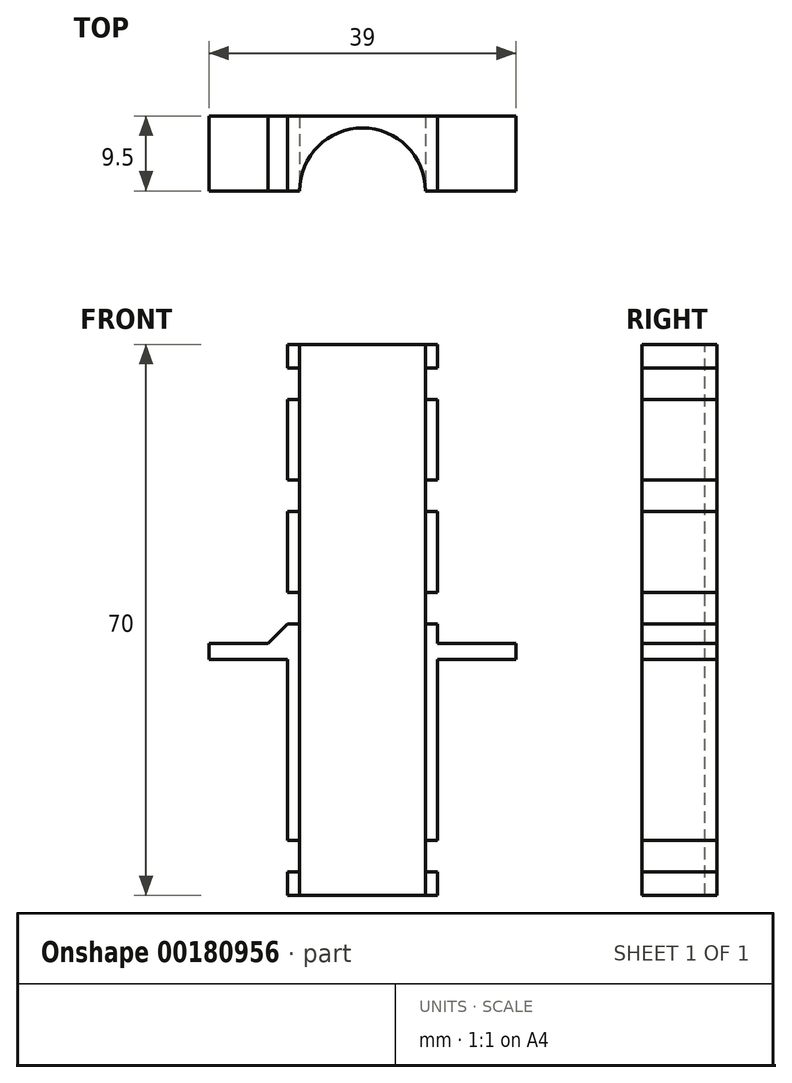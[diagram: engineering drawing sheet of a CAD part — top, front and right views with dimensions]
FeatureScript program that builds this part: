
annotation { "Feature Type Name" : "Feature", "Feature Type Description" : "" }
export const myFeature = defineFeature(function(context is Context, id is Id, definition is map)
    precondition{}
    {
        {
            var Q0;
            Q0=qCreatedBy(makeId("Top.planeOp"),FACE);
            var sketch = newSketch(context, id + "F0", { "sketchPlane" : qUnion([Q0])});
            skArc(sketch, "E0", {"start": v(-8, 0) * mm, "mid": v(0, 8) * mm, "end": v(8, 0) * mm});
            skLineSegment(sketch, "E1", {"start": v(-8, 0) * mm, "end": v(-9.5, 0) * mm});
            skLineSegment(sketch, "E2", {"start": v(8, 0) * mm, "end": v(9.5, 0) * mm});
            skLineSegment(sketch, "E3", {"start": v(-9.5, 0) * mm, "end": v(-9.5, 9.5) * mm});
            skLineSegment(sketch, "E4", {"start": v(-9.5, 9.5) * mm, "end": v(9.5, 9.5) * mm});
            skLineSegment(sketch, "E5", {"start": v(9.5, 9.5) * mm, "end": v(9.5, 0) * mm});
            skSolve(sketch);
        }
        {
            var Q0;
            Q0=qSketchRegion(id+"F0",true);
            extrude(context, id + "F1", {"entities" : qUnion([Q0]), "oppositeDirection" : true, "depth" : 40 * mm});
        }
        {
            var Q0;
            Q0=qCreatedBy(makeId("Top.planeOp"),FACE);
            cPlane(context, id + "F2", {"entities" : qUnion([Q0]), "cplaneType" : CPlaneType.OFFSET, "offset" : 10 * mm, "oppositeDirection" : true, "width" : 150 * mm, "height" : 150 * mm});
        }
        {
            var Q0;
            Q0=qCreatedBy(id+"F2.planeOp",FACE);
            var sketch = newSketch(context, id + "F3", { "sketchPlane" : qUnion([Q0])});
            skLineSegment(sketch, "E6.bottom", {"start": v(-9.5, 0) * mm, "end": v(-19.5, 0) * mm});
            skLineSegment(sketch, "E6.top", {"start": v(-9.5, 9.5) * mm, "end": v(-19.5, 9.5) * mm});
            skLineSegment(sketch, "E6.left", {"start": v(-9.5, 0) * mm, "end": v(-9.5, 9.5) * mm});
            skLineSegment(sketch, "E6.right", {"start": v(-19.5, 0) * mm, "end": v(-19.5, 9.5) * mm});
            skLineSegment(sketch, "E7.MirrorCS", {"start": v(9.5, 0) * mm, "end": v(19.5, 0) * mm});
            skLineSegment(sketch, "E8.MirrorCS", {"start": v(19.5, 0) * mm, "end": v(19.5, 9.5) * mm});
            skLineSegment(sketch, "E9.MirrorCS", {"start": v(9.5, 9.5) * mm, "end": v(19.5, 9.5) * mm});
            skLineSegment(sketch, "E10.MirrorCS", {"start": v(9.5, 0) * mm, "end": v(9.5, 9.5) * mm});
            skPoint(sketch, "E11", {"position": v(0, 0) * mm});
            skSolve(sketch);
        }
        {
            var Q0;
            Q0=qSketchRegion(id+"F3",true);
            extrude(context, id + "F4", {"entities" : qUnion([Q0]), "operationType" : NewBodyOperationType.ADD, "depth" : 2 * mm});
        }
        {
            var Q0;
            Q0=makeQuery(id+"F1.opExtrude","CAP_FACE",FACE,{"disambiguationData":[OSD([sQuery(id+"F0.wireOp",EDGE,"E0"),sQuery(id+"F0.wireOp",EDGE,"E1"),sQuery(id+"F0.wireOp",EDGE,"E2"),sQuery(id+"F0.wireOp",EDGE,"E3"),sQuery(id+"F0.wireOp",EDGE,"E4"),sQuery(id+"F0.wireOp",EDGE,"E5")])],"isStart":true});
            extrude(context, id + "F5", {"entities" : qUnion([Q0]), "operationType" : NewBodyOperationType.ADD, "depth" : 30 * mm});
        }
        {
            var Q0;
            {var subQ0=sQuery(id+"F3.wireOp",EDGE,"E6.left");var subQ2=sQuery(id+"F0.wireOp",EDGE,"E1");Q0=makeQuery(id+"F4.boolean.opBoolean","SPLIT",FACE,{"disambiguationData":[TD([makeQuery(id+"F4.opExtrude","CAP_FACE",FACE,{"disambiguationData":[OSD([sQuery(id+"F3.wireOp",EDGE,"E6.bottom"),sQuery(id+"F3.wireOp",EDGE,"E6.top"),subQ0,sQuery(id+"F3.wireOp",EDGE,"E6.right")])],"isStart":true})])],"derivedFrom":makeQuery(id+"F1.opExtrude","SWEPT_FACE",FACE,{"disambiguationData":[OSD([subQ2])]})});}
            var sketch = newSketch(context, id + "F6", { "sketchPlane" : qUnion([Q0])});
            skLineSegment(sketch, "E12.bottom", {"start": v(-9.5, -1.5) * mm, "end": v(-8, -1.5) * mm});
            skLineSegment(sketch, "E12.top", {"start": v(-9.5, -5.5) * mm, "end": v(-8, -5.5) * mm});
            skLineSegment(sketch, "E12.left", {"start": v(-9.5, -1.5) * mm, "end": v(-9.5, -5.5) * mm});
            skLineSegment(sketch, "E12.right", {"start": v(-8, -1.5) * mm, "end": v(-8, -5.5) * mm});
            skPoint(sketch, "E13", {"position": v(-9.5, -3.5) * mm});
            skLineSegment(sketch, "E14.bottom", {"start": v(-9.5, -37) * mm, "end": v(-8, -37) * mm});
            skLineSegment(sketch, "E14.top", {"start": v(-9.5, -33) * mm, "end": v(-8, -33) * mm});
            skLineSegment(sketch, "E14.left", {"start": v(-9.5, -37) * mm, "end": v(-9.5, -33) * mm});
            skLineSegment(sketch, "E14.right", {"start": v(-8, -37) * mm, "end": v(-8, -33) * mm});
            skLineSegment(sketch, "E15", {"start": v(-8, -37) * mm, "end": v(-8, -40) * mm, "construction": true});
            skLineSegment(sketch, "E16.MirrorCS", {"start": v(9.5, -1.5) * mm, "end": v(8, -1.5) * mm});
            skLineSegment(sketch, "E17.MirrorCS", {"start": v(8, -1.5) * mm, "end": v(8, -5.5) * mm});
            skLineSegment(sketch, "E18.MirrorCS", {"start": v(9.5, -5.5) * mm, "end": v(8, -5.5) * mm});
            skLineSegment(sketch, "E19.MirrorCS", {"start": v(8, -37) * mm, "end": v(8, -33) * mm});
            skLineSegment(sketch, "E20.MirrorCS", {"start": v(9.5, -33) * mm, "end": v(8, -33) * mm});
            skLineSegment(sketch, "E21.MirrorCS", {"start": v(9.5, -37) * mm, "end": v(9.5, -33) * mm});
            skLineSegment(sketch, "E22.MirrorCS", {"start": v(9.5, -37) * mm, "end": v(8, -37) * mm});
            skLineSegment(sketch, "E23.bottom", {"start": v(-9.5, 27) * mm, "end": v(-8, 27) * mm});
            skLineSegment(sketch, "E23.top", {"start": v(-9.5, 23) * mm, "end": v(-8, 23) * mm});
            skLineSegment(sketch, "E23.left", {"start": v(-9.5, 27) * mm, "end": v(-9.5, 23) * mm});
            skLineSegment(sketch, "E23.right", {"start": v(-8, 27) * mm, "end": v(-8, 23) * mm});
            skLineSegment(sketch, "E24.MirrorCS", {"start": v(9.5, 23) * mm, "end": v(8, 23) * mm});
            skLineSegment(sketch, "E25.MirrorCS", {"start": v(9.5, 27) * mm, "end": v(9.5, 23) * mm});
            skLineSegment(sketch, "E26.MirrorCS", {"start": v(8, 27) * mm, "end": v(8, 23) * mm});
            skLineSegment(sketch, "E27.MirrorCS", {"start": v(9.5, 27) * mm, "end": v(8, 27) * mm});
            skLineSegment(sketch, "E28.MirrorCS", {"start": v(9.5, -1.5) * mm, "end": v(9.5, -5.5) * mm});
            skLineSegment(sketch, "E29", {"start": v(-9.5, -5.5) * mm, "end": v(-9.5, -8.5) * mm, "construction": true});
            skLineSegment(sketch, "E30", {"start": v(-8.75, 23) * mm, "end": v(-8.75, -1.5) * mm, "construction": true});
            skLineSegment(sketch, "E31.bottom", {"start": v(-9.5, 12.75) * mm, "end": v(-8, 12.75) * mm});
            skLineSegment(sketch, "E31.top", {"start": v(-9.5, 8.75) * mm, "end": v(-8, 8.75) * mm});
            skLineSegment(sketch, "E31.left", {"start": v(-9.5, 12.75) * mm, "end": v(-9.5, 8.75) * mm});
            skLineSegment(sketch, "E31.right", {"start": v(-8, 12.75) * mm, "end": v(-8, 8.75) * mm});
            skPoint(sketch, "E31.middle", {"position": v(-8.75, 10.75) * mm});
            skLineSegment(sketch, "E32.MirrorCS", {"start": v(9.5, 8.75) * mm, "end": v(8, 8.75) * mm});
            skPoint(sketch, "E33.MirrorP", {"position": v(8.75, 10.75) * mm});
            skLineSegment(sketch, "E34.MirrorCS", {"start": v(9.5, 12.75) * mm, "end": v(8, 12.75) * mm});
            skLineSegment(sketch, "E35.MirrorCS", {"start": v(9.5, 12.75) * mm, "end": v(9.5, 8.75) * mm});
            skLineSegment(sketch, "E36.MirrorCS", {"start": v(8, 12.75) * mm, "end": v(8, 8.75) * mm});
            skSolve(sketch);
        }
        {
            var Q0;
            Q0=qSketchRegion(id+"F6",true);
            extrude(context, id + "F7", {"entities" : qUnion([Q0]), "operationType" : NewBodyOperationType.REMOVE, "endBound" : BoundingType.THROUGH_ALL, "oppositeDirection" : true, "depth" : 25 * mm});
        }
        {
            var Q0;
            {var subQ0=sQuery(id+"F3.wireOp",EDGE,"E6.left");Q0=makeQuery(id+"F4.boolean.opBoolean","SPLIT",EDGE,{"disambiguationData":[TD([makeQuery(id+"F1.opExtrude","SWEPT_FACE",FACE,{"disambiguationData":[OSD([sQuery(id+"F0.wireOp",EDGE,"E4")])]})])],"derivedFrom":makeQuery(id+"F4.opExtrude","CAP_EDGE",EDGE,{"disambiguationData":[OSD([subQ0])],"isStart":false})});}
            var Q1;
            {var subQ0=sQuery(id+"F3.wireOp",EDGE,"E10.MirrorCS");Q1=makeQuery(id+"F4.boolean.opBoolean","SPLIT",EDGE,{"disambiguationData":[TD([makeQuery(id+"F1.opExtrude","SWEPT_FACE",FACE,{"disambiguationData":[OSD([sQuery(id+"F0.wireOp",EDGE,"E4")])]})])],"derivedFrom":makeQuery(id+"F4.opExtrude","CAP_EDGE",EDGE,{"disambiguationData":[OSD([subQ0])],"isStart":false})});}
            chamfer(context, id + "F8", {"entities" : qUnion([Q0, Q1]), "width" : 2.5 * mm, "tangentPropagation" : true});
        }
    });
